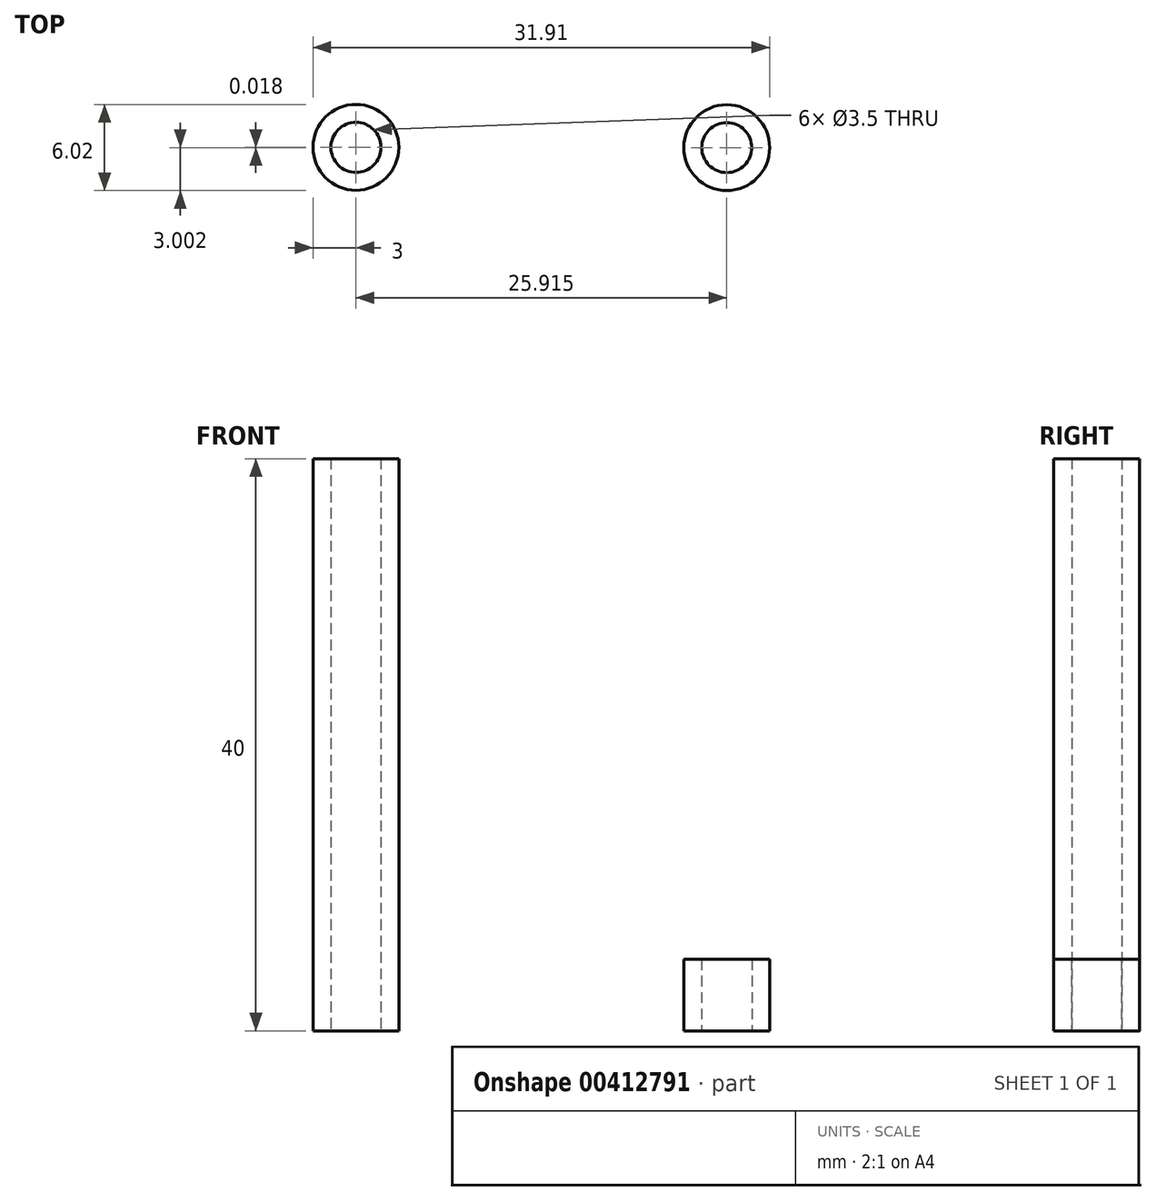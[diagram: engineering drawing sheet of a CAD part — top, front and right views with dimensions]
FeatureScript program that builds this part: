
annotation { "Feature Type Name" : "Feature", "Feature Type Description" : "" }
export const myFeature = defineFeature(function(context is Context, id is Id, definition is map)
    precondition{}
    {
        {
            var Q0;
            Q0=qCreatedBy(makeId("Top.planeOp"),FACE);
            var sketch = newSketch(context, id + "F0", { "sketchPlane" : qUnion([Q0])});
            skCircle(sketch, "E0", {"center": v(-16.84, 4.9) * mm, "radius": 3 * mm});
            skCircle(sketch, "E1", {"center": v(-16.84, 4.9) * mm, "radius": 1.75 * mm});
            skSolve(sketch);
        }
        {
            var Q0;
            Q0=makeQuery(id+"F0.imprint","IMPRINT",FACE,{"disambiguationData":[TD([[makeQuery(id+"F0.imprint","IMPRINT",EDGE,{"derivedFrom":sQuery(id+"F0.wireOp",EDGE,"E0")}),1.0]])]});
            extrude(context, id + "F1", {"entities" : qUnion([Q0]), "depth" : 40 * mm});
        }
        {
            var Q0;
            Q0=qCreatedBy(makeId("Top.planeOp"),FACE);
            var sketch = newSketch(context, id + "F2", { "sketchPlane" : qUnion([Q0])});
            skCircle(sketch, "E2", {"center": v(9.07, 4.87) * mm, "radius": 3 * mm});
            skCircle(sketch, "E3", {"center": v(9.07, 4.87) * mm, "radius": 1.75 * mm});
            skSolve(sketch);
        }
        {
            var Q0;
            Q0=qSketchRegion(id+"F2",true);
            extrude(context, id + "F3", {"entities" : qUnion([Q0]), "depth" : 5 * mm});
        }
    });
